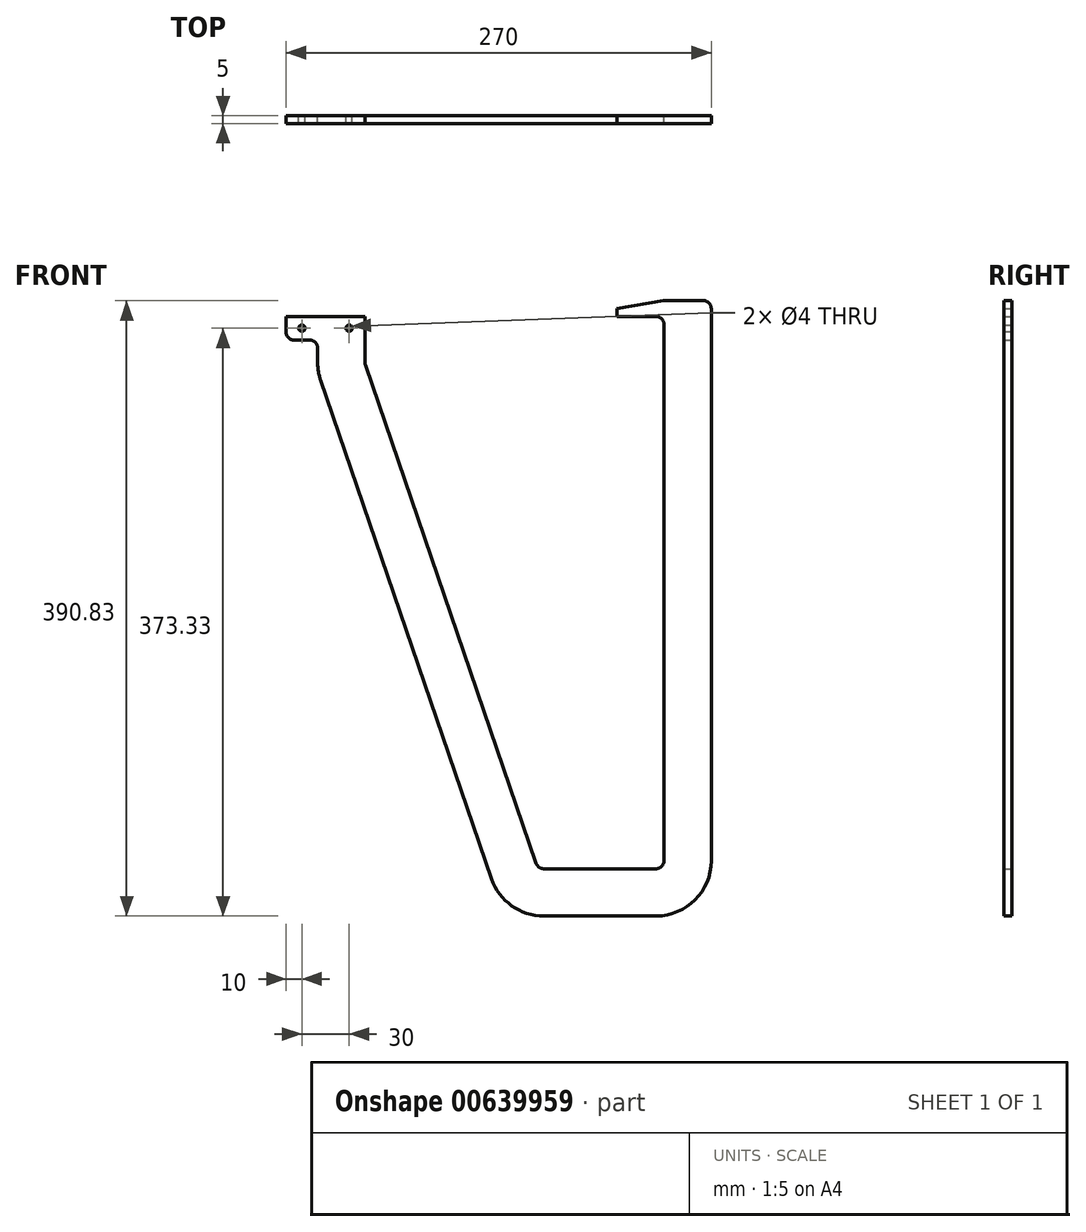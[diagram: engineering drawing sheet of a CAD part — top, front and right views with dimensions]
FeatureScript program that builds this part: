
annotation { "Feature Type Name" : "Feature", "Feature Type Description" : "" }
export const myFeature = defineFeature(function(context is Context, id is Id, definition is map)
    precondition{}
    {
        {
            var Q0;
            Q0=qCreatedBy(makeId("Front.planeOp"),FACE);
            var sketch = newSketch(context, id + "F0", { "sketchPlane" : qUnion([Q0])});
            skLineSegment(sketch, "E0", {"start": v(0, 0) * mm, "end": v(0, -350.83) * mm});
            skLineSegment(sketch, "E1", {"start": v(0, -350.83) * mm, "end": v(-80, -350.83) * mm});
            skLineSegment(sketch, "E2", {"start": v(-80, -350.83) * mm, "end": v(-190, -30) * mm});
            skLineSegment(sketch, "E3", {"start": v(-220, -35) * mm, "end": v(-101.43, -380.83) * mm});
            skLineSegment(sketch, "E4", {"start": v(-101.43, -380.83) * mm, "end": v(30, -380.83) * mm});
            skLineSegment(sketch, "E5", {"start": v(30, -380.83) * mm, "end": v(30, 10) * mm});
            skLineSegment(sketch, "E6", {"start": v(30, 10) * mm, "end": v(0, 10) * mm});
            skLineSegment(sketch, "E7", {"start": v(0, 10) * mm, "end": v(-30, 5) * mm});
            skLineSegment(sketch, "E8", {"start": v(-30, 5) * mm, "end": v(-30, 0) * mm});
            skLineSegment(sketch, "E9", {"start": v(-30, 0) * mm, "end": v(0, 0) * mm});
            skLineSegment(sketch, "E10", {"start": v(0, -350.83) * mm, "end": v(30, -350.83) * mm, "construction": true});
            skLineSegment(sketch, "E11", {"start": v(-80, -350.83) * mm, "end": v(-108.38, -360.56) * mm, "construction": true});
            skLineSegment(sketch, "E12", {"start": v(0, -350.83) * mm, "end": v(0, -380.83) * mm, "construction": true});
            skLineSegment(sketch, "E13", {"start": v(-190, -30) * mm, "end": v(-190, 0) * mm});
            skLineSegment(sketch, "E14", {"start": v(-190, 0) * mm, "end": v(-240, 0) * mm});
            skLineSegment(sketch, "E15", {"start": v(-240, 0) * mm, "end": v(-240, -15) * mm});
            skLineSegment(sketch, "E16", {"start": v(-240, -15) * mm, "end": v(-220, -15) * mm});
            skLineSegment(sketch, "E17", {"start": v(-220, -15) * mm, "end": v(-220, -35) * mm});
            skLineSegment(sketch, "E18", {"start": v(-220, -15) * mm, "end": v(-190, -15) * mm, "construction": true});
            skSolve(sketch);
        }
        {
            var Q0;
            Q0 = qSketchRegion(id + "F0", true);
            extrude(context, id + "F1", {"entities" : qUnion([Q0]), "depth" : 5 * mm, "offsetDistance" : 25 * mm, "symmetric" : true});
        }
        {
            var Q0;
            Q0=makeQuery(id+"F1.opExtrude","SWEPT_EDGE",EDGE,{"disambiguationData":[OSD([sQuery(id+"F0.wireOp",EDGE,"E15"),sQuery(id+"F0.wireOp",EDGE,"E16")])]});
            var Q1;
            Q1=makeQuery(id+"F1.opExtrude","SWEPT_EDGE",EDGE,{"disambiguationData":[OSD([sQuery(id+"F0.wireOp",EDGE,"E16"),sQuery(id+"F0.wireOp",EDGE,"E17")])]});
            var Q2;
            Q2=makeQuery(id+"F1.opExtrude","SWEPT_EDGE",EDGE,{"disambiguationData":[OSD([sQuery(id+"F0.wireOp",EDGE,"E5"),sQuery(id+"F0.wireOp",EDGE,"E6")])]});
            var Q3;
            Q3=makeQuery(id+"F1.opExtrude","SWEPT_EDGE",EDGE,{"disambiguationData":[OSD([sQuery(id+"F0.wireOp",EDGE,"E6"),sQuery(id+"F0.wireOp",EDGE,"E7")])]});
            var Q4;
            Q4=makeQuery(id+"F1.opExtrude","SWEPT_EDGE",EDGE,{"disambiguationData":[OSD([sQuery(id+"F0.wireOp",EDGE,"E0"),sQuery(id+"F0.wireOp",EDGE,"E9")])]});
            var Q5;
            Q5=makeQuery(id+"F1.opExtrude","SWEPT_EDGE",EDGE,{"disambiguationData":[OSD([sQuery(id+"F0.wireOp",EDGE,"E0"),sQuery(id+"F0.wireOp",EDGE,"E1")])]});
            var Q6;
            Q6=makeQuery(id+"F1.opExtrude","SWEPT_EDGE",EDGE,{"disambiguationData":[OSD([sQuery(id+"F0.wireOp",EDGE,"E1"),sQuery(id+"F0.wireOp",EDGE,"E2")])]});
            var Q7;
            Q7=makeQuery(id+"F1.opExtrude","SWEPT_EDGE",EDGE,{"disambiguationData":[OSD([sQuery(id+"F0.wireOp",EDGE,"E2"),sQuery(id+"F0.wireOp",EDGE,"E13")])]});
            fillet(context, id + "F2", {"entities" : qUnion([Q0, Q1, Q2, Q3, Q4, Q5, Q6, Q7]), "radius" : 5 * mm, "tangentPropagation" : true, "allowEdgeOverflow" : false});
        }
        {
            var Q0;
            Q0=makeQuery(id+"F1.opExtrude","SWEPT_EDGE",EDGE,{"disambiguationData":[OSD([sQuery(id+"F0.wireOp",EDGE,"E3"),sQuery(id+"F0.wireOp",EDGE,"E17")])]});
            var Q1;
            Q1=makeQuery(id+"F1.opExtrude","SWEPT_EDGE",EDGE,{"disambiguationData":[OSD([sQuery(id+"F0.wireOp",EDGE,"E3"),sQuery(id+"F0.wireOp",EDGE,"E4")])]});
            var Q2;
            Q2=makeQuery(id+"F1.opExtrude","SWEPT_EDGE",EDGE,{"disambiguationData":[OSD([sQuery(id+"F0.wireOp",EDGE,"E4"),sQuery(id+"F0.wireOp",EDGE,"E5")])]});
            fillet(context, id + "F3", {"entities" : qUnion([Q0, Q1, Q2]), "radius" : 35 * mm, "tangentPropagation" : true, "allowEdgeOverflow" : false});
        }
        {
            var Q0;
            Q0=qCreatedBy(makeId("Front.planeOp"),FACE);
            var sketch = newSketch(context, id + "F4", { "sketchPlane" : qUnion([Q0])});
            skCircle(sketch, "E19", {"center": v(-230, -7.5) * mm, "radius": 2 * mm});
            skCircle(sketch, "E20", {"center": v(-200, -7.5) * mm, "radius": 2 * mm});
            skLineSegment(sketch, "E21.bottom", {"start": v(-190, -15) * mm, "end": v(-240, -15) * mm, "construction": true});
            skLineSegment(sketch, "E21.top", {"start": v(-190, 0) * mm, "end": v(-240, 0) * mm, "construction": true});
            skLineSegment(sketch, "E21.left", {"start": v(-190, -15) * mm, "end": v(-190, 0) * mm, "construction": true});
            skLineSegment(sketch, "E21.right", {"start": v(-240, -15) * mm, "end": v(-240, 0) * mm, "construction": true});
            skPoint(sketch, "E21.middle", {"position": v(-215, -7.5) * mm});
            skLineSegment(sketch, "E22", {"start": v(-230, -7.5) * mm, "end": v(-200, -7.5) * mm, "construction": true});
            skSolve(sketch);
        }
        {
            var Q0;
            Q0 = qSketchRegion(id + "F4", true);
            extrude(context, id + "F5", {"entities" : qUnion([Q0]), "operationType" : NewBodyOperationType.REMOVE, "endBound" : BoundingType.UP_TO_NEXT, "depth" : 25 * mm, "offsetDistance" : 25 * mm, "hasSecondDirection" : true, "secondDirectionBound" : BoundingType.UP_TO_NEXT, "secondDirectionOppositeDirection" : true, "secondDirectionDepth" : 25 * mm});
        }
    });
